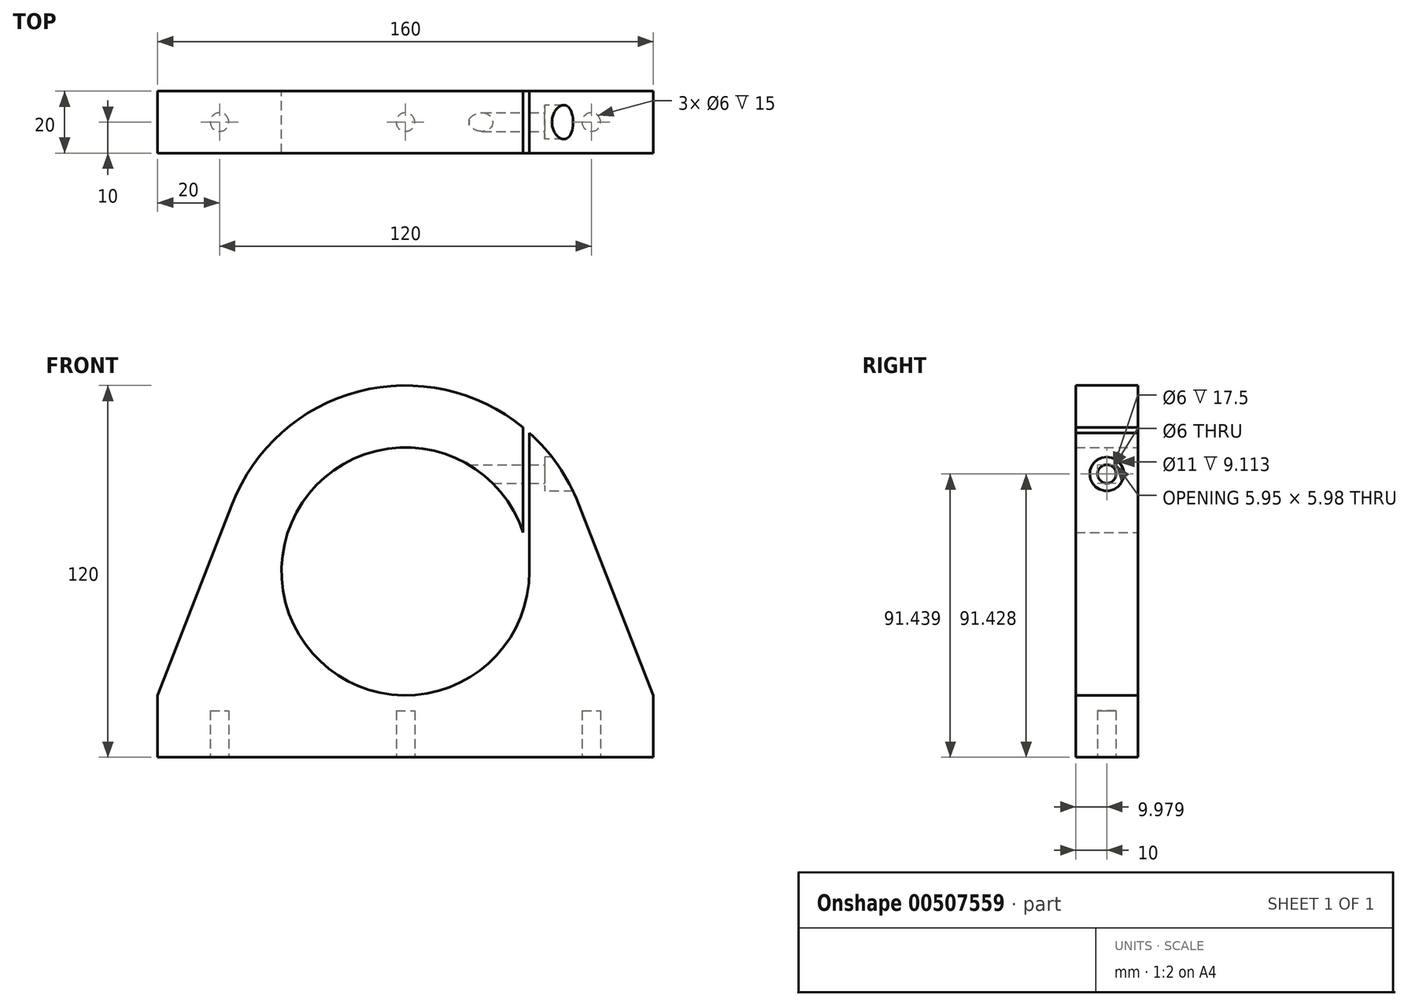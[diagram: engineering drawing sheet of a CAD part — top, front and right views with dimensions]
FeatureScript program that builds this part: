
annotation { "Feature Type Name" : "Feature", "Feature Type Description" : "" }
export const myFeature = defineFeature(function(context is Context, id is Id, definition is map)
    precondition{}
    {
        {
            var Q0;
            Q0=qCreatedBy(makeId("Front.planeOp"),FACE);
            var sketch = newSketch(context, id + "F0", { "sketchPlane" : qUnion([Q0])});
            skLineSegment(sketch, "E0.bottom", {"start": v(0, 0) * mm, "end": v(160, 0) * mm});
            skLineSegment(sketch, "E0.left", {"start": v(0, 0) * mm, "end": v(0, 20) * mm});
            skLineSegment(sketch, "E0.right", {"start": v(160, 0) * mm, "end": v(160, 20) * mm});
            skCircle(sketch, "E1", {"center": v(80, 60) * mm, "radius": 40 * mm});
            skArc(sketch, "E2", {"start": v(135.9, 81.8) * mm, "mid": v(80, 120) * mm, "end": v(24.1, 81.8) * mm});
            skLineSegment(sketch, "E3", {"start": v(0, 20) * mm, "end": v(24.1, 81.8) * mm});
            skLineSegment(sketch, "E4", {"start": v(160, 20) * mm, "end": v(135.9, 81.8) * mm});
            skSolve(sketch);
        }
        {
            var Q0;
            Q0=makeQuery(id+"F0.imprint","IMPRINT",FACE,{"disambiguationData":[TD([[makeQuery(id+"F0.imprint","IMPRINT",EDGE,{"derivedFrom":sQuery(id+"F0.wireOp",EDGE,"E0.bottom")}),1.0]])]});
            extrude(context, id + "F1", {"entities" : qUnion([Q0]), "depth" : 20 * mm, "offsetDistance" : 25 * mm});
        }
        {
            var Q0;
            Q0=makeQuery(id+"F1.opExtrude","CAP_FACE",FACE,{"disambiguationData":[OSD([sQuery(id+"F0.wireOp",EDGE,"E0.bottom"),sQuery(id+"F0.wireOp",EDGE,"E1"),sQuery(id+"F0.wireOp",EDGE,"E2"),sQuery(id+"F0.wireOp",EDGE,"E0.left"),sQuery(id+"F0.wireOp",EDGE,"E3"),sQuery(id+"F0.wireOp",EDGE,"E0.right"),sQuery(id+"F0.wireOp",EDGE,"E4")])],"isStart":false});
            var sketch = newSketch(context, id + "F2", { "sketchPlane" : qUnion([Q0])});
            skLineSegment(sketch, "E5", {"start": v(80, 60) * mm, "end": v(120, 60) * mm});
            skLineSegment(sketch, "E6", {"start": v(120, 60) * mm, "end": v(120, 117.27) * mm});
            skLineSegment(sketch, "E7", {"start": v(120, 117.27) * mm, "end": v(118, 117.41) * mm});
            skLineSegment(sketch, "E8", {"start": v(118, 117.41) * mm, "end": v(118, 60) * mm});
            skSolve(sketch);
        }
        {
            var Q0;
            Q0 = qSketchRegion(id + "F2", true);
            extrude(context, id + "F3", {"entities" : qUnion([Q0]), "operationType" : NewBodyOperationType.REMOVE, "oppositeDirection" : true, "depth" : 25 * mm, "offsetDistance" : 25 * mm});
        }
        {
            var Q0;
            Q0=makeQuery(id+"F3.boolean.opBoolean","COPY",FACE,{"derivedFrom":makeQuery(id+"F3.opExtrude","SWEPT_FACE",FACE,{"disambiguationData":[OSD([sQuery(id+"F2.wireOp",EDGE,"E8")])]})});
            var sketch = newSketch(context, id + "F4", { "sketchPlane" : qUnion([Q0])});
            skCircle(sketch, "E9", {"center": v(-10, 91.43) * mm, "radius": 3 * mm});
            skPoint(sketch, "E9.centerSnap0", {"position": v(0, 91.43) * mm});
            skSolve(sketch);
        }
        {
            var Q0;
            Q0 = qSketchRegion(id + "F4", true);
            extrude(context, id + "F5", {"entities" : qUnion([Q0]), "operationType" : NewBodyOperationType.REMOVE, "oppositeDirection" : true, "depth" : 35 * mm, "offsetDistance" : 25 * mm, "symmetric" : true});
        }
        {
            var Q0;
            Q0=makeQuery(id+"F3.boolean.opBoolean","COPY",FACE,{"derivedFrom":makeQuery(id+"F3.opExtrude","SWEPT_FACE",FACE,{"disambiguationData":[OSD([sQuery(id+"F2.wireOp",EDGE,"E6")])]})});
            cPlane(context, id + "F6", {"entities" : qUnion([Q0]), "cplaneType" : CPlaneType.OFFSET, "offset" : 5 * mm, "oppositeDirection" : true, "width" : 150 * mm, "height" : 150 * mm});
        }
        {
            var Q0;
            Q0=qCreatedBy(id+"F6.planeOp",FACE);
            var sketch = newSketch(context, id + "F7", { "sketchPlane" : qUnion([Q0])});
            skCircle(sketch, "E10", {"center": v(10, 91.43) * mm, "radius": 5.5 * mm});
            skSolve(sketch);
        }
        {
            var Q0;
            Q0 = qSketchRegion(id + "F7", true);
            extrude(context, id + "F8", {"entities" : qUnion([Q0]), "operationType" : NewBodyOperationType.REMOVE, "oppositeDirection" : true, "depth" : 25 * mm, "offsetDistance" : 25 * mm});
        }
        {
            var Q0;
            Q0=makeQuery(id+"F1.opExtrude","SWEPT_FACE",FACE,{"disambiguationData":[OSD([sQuery(id+"F0.wireOp",EDGE,"E0.bottom")])]});
            var sketch = newSketch(context, id + "F9", { "sketchPlane" : qUnion([Q0])});
            skCircle(sketch, "E11", {"center": v(20, 10) * mm, "radius": 3 * mm});
            skCircle(sketch, "E12", {"center": v(140, 10) * mm, "radius": 3 * mm});
            skCircle(sketch, "E13", {"center": v(80, 10) * mm, "radius": 3 * mm});
            skSolve(sketch);
        }
        {
            var Q0;
            Q0 = qSketchRegion(id + "F9", true);
            extrude(context, id + "F10", {"entities" : qUnion([Q0]), "operationType" : NewBodyOperationType.REMOVE, "oppositeDirection" : true, "depth" : 15 * mm, "offsetDistance" : 25 * mm});
        }
    });
